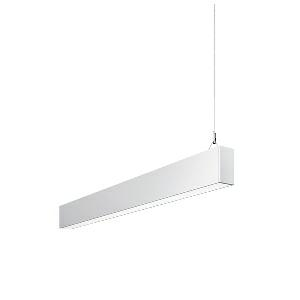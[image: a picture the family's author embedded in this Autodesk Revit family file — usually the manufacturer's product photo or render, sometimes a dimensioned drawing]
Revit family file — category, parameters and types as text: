
# Revit family: dotoo_line_-_dlp_1500_840_d_end_00805779_c763
name_source: partatom
category: Lighting Fixtures
units: mm (PartAtom-declared; Revit-internal decimal feet)

## family parameters
Cut with Voids When Loaded = No
Host = Face
Light Source = No
Part Type = Normal
Room Calculation Point = No
Round Connector Dimension = Use Diameter
Shared = No

## types (1)
- DOTOO.line - DLP 1500/840/D END (1 x LED, 1350 lm, 4000K)
    Apparent Load = 13 VA
    Approval mark = CE
    CIE Flux Codes = 67 91 98 100 100
    Color Rendering = 80-89
    Color Temperature = 4000K
    Control Gear = Electronic ballast
    Default Elevation = 1800 mm
    Description = DLP 1500/840/D|Suspended luminaire|light source: LED|connected load: 220-240 V, 50/60 Hz|Power consumption: approx. 13 W|standby: approx. 0,20|luminous flux: 1350 lm|luminous efficacy: 103 lm/W|light distribution: Direct|direct ratio: approx. 100 %|colour temperature: Cold white, ca. 4000 K|color rendering index (CRI): >= 80|chromaticity tolerance:  3 SDCM|System of protection: IP 40|technology: Continuously dimmable|luminaire body|material: Sectional aluminium|colour: White|lamp cover: Acrylic (PMMA), Clear|mains lead: 1,0 m With free stranded wires|Fastening: Steel cable 0.3 - 0.7 m|glare control: Prism aperture|luminance(L65): <= 3000 cd/m|unified glare rating(4H 8H): <=  19|special features: DALI Load 1x, TouchDIM - dimming via standard switch, Through-wired, up to 18 m on one mains connection, Flicker-free, Suitable as emergency lighting, Mechanical and electrical connection of the individual modules without tools|
    Frequency = 50 Hz
    Height = 110 mm
    Lamp = 1 x LED
    Lamp Light Flux = 1350 lm
    Lamp count = 1
    Length = 1128 mm
    Luminous efficacy = 104 lm/W
    Manufacturer = Waldmann
    ModVariant = No
    Model = 00805779
    Mounting Place = Ceiling
    Mounting Type = Pendant
    Number of Poles = 1
    OnlyDefault = Yes
    Power Factor = 1
    Product Name = DOTOO.line - DLP 1500/840/D END
    Product group = Suspended luminaire
    ProductGroupID = 9
    Protection Class = Protection class I
    Protection Degree = IP 40
    RLX_Detail_Level = 1
    RLX_Emergency_Light_Flux = 0 lm
    RLX_Emergency_Type = 0
    RLX_Emergency_Type_DB = No
    RlxData = <blob elided: 18321 chars, md5=33490bb0>
    Socket = socket
    Standby Power = 0 W
    System Light Flux = 1350 lm
    System Power = 13 W
    Type Comments = Product without accessories
    Type Image = 113303000-00692573.jpg
    URL = http://relux.com
    VarID = ---
    Voltage = 230 V
    Voltage Range = 220-240 V
    Weight = 0.00 kg
    Width = 60 mm  [stored 0.19685 ft]

note: [stored X ft] marks values corroborated as IEEE doubles in the binary element streams (Revit-internal decimal feet)

## geometry (parser evidence)
native form markers: Blend x4, Sweep x10
no freeform markers — native parametric forms only
